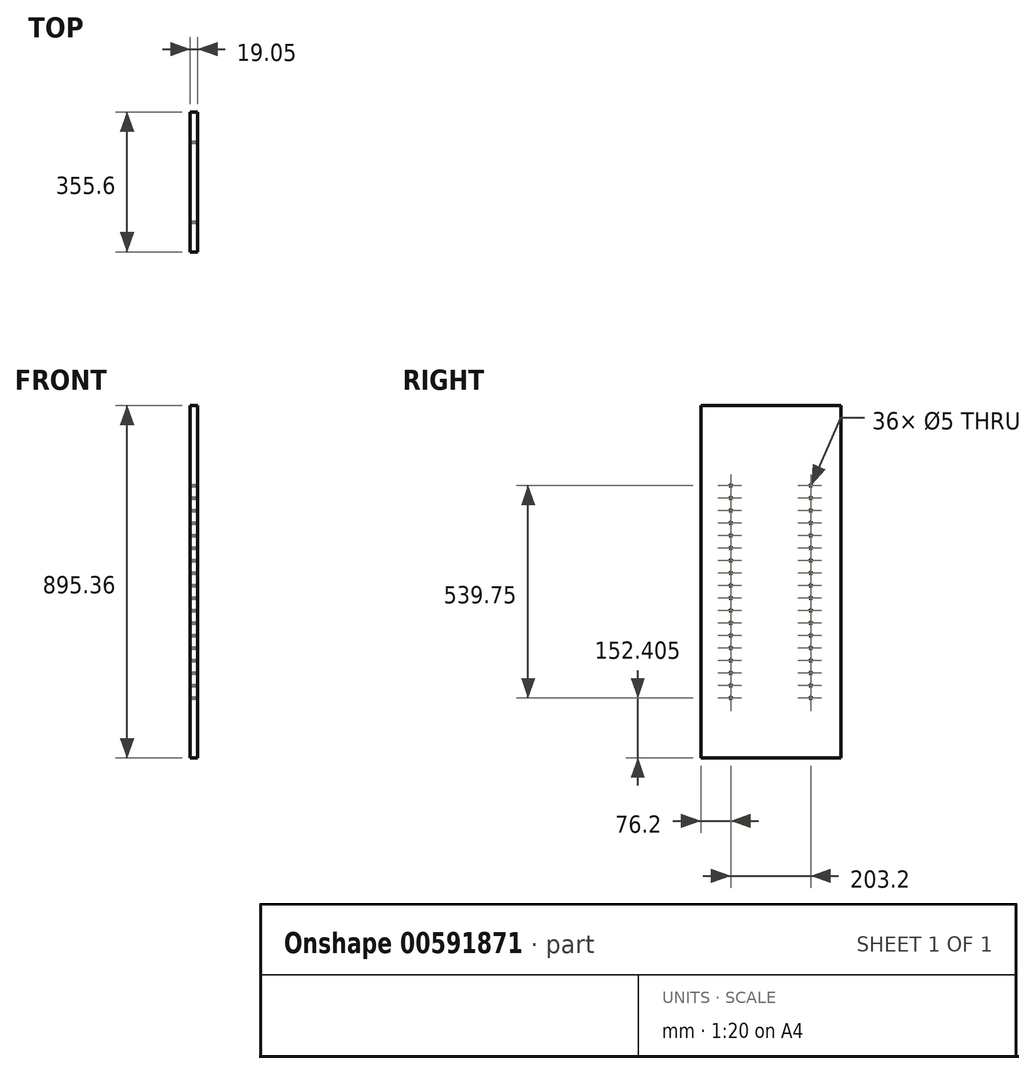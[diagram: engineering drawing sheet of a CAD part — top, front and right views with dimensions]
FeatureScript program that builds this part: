
annotation { "Feature Type Name" : "Feature", "Feature Type Description" : "" }
export const myFeature = defineFeature(function(context is Context, id is Id, definition is map)
    precondition{}
    {
        {
            var Q0;
            Q0=qCreatedBy(makeId("Right.planeOp"),FACE);
            var sketch = newSketch(context, id + "F0", { "sketchPlane" : qUnion([Q0])});
            skLineSegment(sketch, "E0.bottom", {"start": v(177.8, 447.68) * mm, "end": v(-177.8, 447.68) * mm});
            skLineSegment(sketch, "E0.top", {"start": v(177.8, -447.68) * mm, "end": v(-177.8, -447.68) * mm});
            skLineSegment(sketch, "E0.left", {"start": v(177.8, 447.68) * mm, "end": v(177.8, -447.68) * mm});
            skLineSegment(sketch, "E0.right", {"start": v(-177.8, 447.68) * mm, "end": v(-177.8, -447.68) * mm});
            skPoint(sketch, "E0.middle", {"position": v(0, 0) * mm});
            skSolve(sketch);
        }
        {
            var Q0;
            Q0=makeQuery(id+"F0.imprint","IMPRINT",FACE,{"disambiguationData":[TD([[makeQuery(id+"F0.imprint","IMPRINT",EDGE,{"derivedFrom":sQuery(id+"F0.wireOp",EDGE,"E0.bottom")}),1.0]])]});
            extrude(context, id + "F1", {"entities" : qUnion([Q0]), "depth" : 19.05 * mm, "offsetDistance" : 25.4 * mm});
        }
        {
            var Q0;
            Q0=makeQuery(id+"F1.opExtrude","CAP_FACE",FACE,{"disambiguationData":[OSD([sQuery(id+"F0.wireOp",EDGE,"E0.bottom"),sQuery(id+"F0.wireOp",EDGE,"E0.top"),sQuery(id+"F0.wireOp",EDGE,"E0.left"),sQuery(id+"F0.wireOp",EDGE,"E0.right")])],"isStart":false});
            var sketch = newSketch(context, id + "F2", { "sketchPlane" : qUnion([Q0])});
            skLineSegment(sketch, "E1", {"start": v(0, 447.68) * mm, "end": v(0, 212.73) * mm});
            skLineSegment(sketch, "E2.bottom", {"start": v(101.6, 244.48) * mm, "end": v(-101.6, 244.47) * mm});
            skLineSegment(sketch, "E2.top", {"start": v(101.6, 180.98) * mm, "end": v(-101.6, 180.98) * mm});
            skLineSegment(sketch, "E2.left", {"start": v(101.6, 244.48) * mm, "end": v(101.6, 180.98) * mm});
            skLineSegment(sketch, "E2.right", {"start": v(-101.6, 244.48) * mm, "end": v(-101.6, 180.98) * mm});
            skPoint(sketch, "E2.middle", {"position": v(0, 212.73) * mm});
            skLineSegment(sketch, "E3", {"start": v(0, 180.98) * mm, "end": v(0, 117.48) * mm});
            skLineSegment(sketch, "E4.bottom", {"start": v(101.6, 85.73) * mm, "end": v(-101.6, 85.73) * mm});
            skLineSegment(sketch, "E4.top", {"start": v(101.6, 149.23) * mm, "end": v(-101.6, 149.23) * mm});
            skLineSegment(sketch, "E4.left", {"start": v(101.6, 85.73) * mm, "end": v(101.6, 149.23) * mm});
            skLineSegment(sketch, "E4.right", {"start": v(-101.6, 85.73) * mm, "end": v(-101.6, 149.23) * mm});
            skPoint(sketch, "E4.middle", {"position": v(0, 117.48) * mm});
            skLineSegment(sketch, "E5", {"start": v(0, 85.73) * mm, "end": v(0, 22.23) * mm});
            skLineSegment(sketch, "E6.bottom", {"start": v(101.6, -9.52) * mm, "end": v(-101.6, -9.52) * mm});
            skLineSegment(sketch, "E6.top", {"start": v(101.6, 53.98) * mm, "end": v(-101.6, 53.98) * mm});
            skLineSegment(sketch, "E6.left", {"start": v(101.6, -9.52) * mm, "end": v(101.6, 53.98) * mm});
            skLineSegment(sketch, "E6.right", {"start": v(-101.6, -9.52) * mm, "end": v(-101.6, 53.98) * mm});
            skPoint(sketch, "E6.middle", {"position": v(0, 22.23) * mm});
            skLineSegment(sketch, "E7", {"start": v(0, -9.52) * mm, "end": v(0, -73.02) * mm});
            skLineSegment(sketch, "E8.bottom", {"start": v(101.6, -104.77) * mm, "end": v(-101.6, -104.77) * mm});
            skLineSegment(sketch, "E8.top", {"start": v(101.6, -41.27) * mm, "end": v(-101.6, -41.27) * mm});
            skLineSegment(sketch, "E8.left", {"start": v(101.6, -104.77) * mm, "end": v(101.6, -41.27) * mm});
            skLineSegment(sketch, "E8.right", {"start": v(-101.6, -104.77) * mm, "end": v(-101.6, -41.27) * mm});
            skPoint(sketch, "E8.middle", {"position": v(0, -73.02) * mm});
            skLineSegment(sketch, "E9", {"start": v(0, -104.77) * mm, "end": v(0, -168.27) * mm});
            skLineSegment(sketch, "E10.bottom", {"start": v(101.6, -200.02) * mm, "end": v(-101.6, -200.02) * mm});
            skLineSegment(sketch, "E10.top", {"start": v(101.6, -136.52) * mm, "end": v(-101.6, -136.52) * mm});
            skLineSegment(sketch, "E10.left", {"start": v(101.6, -200.02) * mm, "end": v(101.6, -136.52) * mm});
            skLineSegment(sketch, "E10.right", {"start": v(-101.6, -200.02) * mm, "end": v(-101.6, -136.52) * mm});
            skPoint(sketch, "E10.middle", {"position": v(0, -168.27) * mm});
            skLineSegment(sketch, "E11", {"start": v(0, -200.02) * mm, "end": v(0, -263.52) * mm});
            skPoint(sketch, "E11.endSnap0", {"position": v(0, -200.02) * mm});
            skLineSegment(sketch, "E12.bottom", {"start": v(101.6, -295.27) * mm, "end": v(-101.6, -295.27) * mm});
            skLineSegment(sketch, "E12.top", {"start": v(101.6, -231.77) * mm, "end": v(-101.6, -231.77) * mm});
            skLineSegment(sketch, "E12.left", {"start": v(101.6, -295.27) * mm, "end": v(101.6, -231.77) * mm});
            skLineSegment(sketch, "E12.right", {"start": v(-101.6, -295.27) * mm, "end": v(-101.6, -231.77) * mm});
            skPoint(sketch, "E12.middle", {"position": v(0, -263.52) * mm});
            skPoint(sketch, "E13", {"position": v(-101.6, 244.47) * mm});
            skPoint(sketch, "E14", {"position": v(-101.6, 212.73) * mm});
            skPoint(sketch, "E15", {"position": v(-101.6, 180.98) * mm});
            skPoint(sketch, "E16", {"position": v(-101.6, 149.23) * mm});
            skPoint(sketch, "E17", {"position": v(-101.6, 117.48) * mm});
            skPoint(sketch, "E18", {"position": v(-101.6, 85.73) * mm});
            skPoint(sketch, "E19", {"position": v(-101.6, 53.98) * mm});
            skPoint(sketch, "E20", {"position": v(-101.6, 22.23) * mm});
            skPoint(sketch, "E21", {"position": v(-101.6, -9.52) * mm});
            skPoint(sketch, "E22", {"position": v(-101.6, -41.27) * mm});
            skPoint(sketch, "E23", {"position": v(-101.6, -73.02) * mm});
            skPoint(sketch, "E24", {"position": v(-101.6, -104.77) * mm});
            skPoint(sketch, "E25", {"position": v(-101.6, -136.52) * mm});
            skPoint(sketch, "E26", {"position": v(-101.6, -168.27) * mm});
            skPoint(sketch, "E27", {"position": v(-101.6, -200.02) * mm});
            skPoint(sketch, "E28", {"position": v(-101.6, -231.77) * mm});
            skPoint(sketch, "E29", {"position": v(-101.6, -263.52) * mm});
            skPoint(sketch, "E30", {"position": v(-101.6, -295.27) * mm});
            skPoint(sketch, "E31", {"position": v(101.6, -295.27) * mm});
            skPoint(sketch, "E32", {"position": v(101.6, -263.52) * mm});
            skPoint(sketch, "E33", {"position": v(101.6, -231.77) * mm});
            skPoint(sketch, "E34", {"position": v(101.6, -200.02) * mm});
            skPoint(sketch, "E35", {"position": v(101.6, -168.27) * mm});
            skPoint(sketch, "E36", {"position": v(101.6, -136.52) * mm});
            skPoint(sketch, "E37", {"position": v(101.6, -104.77) * mm});
            skPoint(sketch, "E38", {"position": v(101.6, -73.02) * mm});
            skPoint(sketch, "E39", {"position": v(101.6, -41.27) * mm});
            skPoint(sketch, "E40", {"position": v(101.6, -9.52) * mm});
            skPoint(sketch, "E41", {"position": v(101.6, 22.23) * mm});
            skPoint(sketch, "E42", {"position": v(101.6, 53.98) * mm});
            skPoint(sketch, "E43", {"position": v(101.6, 85.73) * mm});
            skPoint(sketch, "E44", {"position": v(101.6, 117.48) * mm});
            skPoint(sketch, "E45", {"position": v(101.6, 149.23) * mm});
            skPoint(sketch, "E46", {"position": v(101.6, 180.98) * mm});
            skPoint(sketch, "E47", {"position": v(101.6, 212.73) * mm});
            skPoint(sketch, "E48", {"position": v(101.6, 244.48) * mm});
            skSolve(sketch);
        }
        {
            var Q0;
            Q0=sQuery(id+"F2.wireOp",VERTEX,"E13");
            var Q1;
            Q1=sQuery(id+"F2.wireOp",VERTEX,"E14");
            var Q2;
            Q2=sQuery(id+"F2.wireOp",VERTEX,"E15");
            var Q3;
            Q3=sQuery(id+"F2.wireOp",VERTEX,"E16");
            var Q4;
            Q4=sQuery(id+"F2.wireOp",VERTEX,"E18");
            var Q5;
            Q5=sQuery(id+"F2.wireOp",VERTEX,"E19");
            var Q6;
            Q6=sQuery(id+"F2.wireOp",VERTEX,"E17");
            var Q7;
            Q7=sQuery(id+"F2.wireOp",VERTEX,"E20");
            var Q8;
            Q8=sQuery(id+"F2.wireOp",VERTEX,"E21");
            var Q9;
            Q9=sQuery(id+"F2.wireOp",VERTEX,"E23");
            var Q10;
            Q10=sQuery(id+"F2.wireOp",VERTEX,"E24");
            var Q11;
            Q11=sQuery(id+"F2.wireOp",VERTEX,"E25");
            var Q12;
            Q12=sQuery(id+"F2.wireOp",VERTEX,"E25");
            var Q13;
            Q13=sQuery(id+"F2.wireOp",VERTEX,"E26");
            var Q14;
            Q14=sQuery(id+"F2.wireOp",VERTEX,"E27");
            var Q15;
            Q15=sQuery(id+"F2.wireOp",VERTEX,"E28");
            var Q16;
            Q16=sQuery(id+"F2.wireOp",VERTEX,"E29");
            var Q17;
            Q17=sQuery(id+"F2.wireOp",VERTEX,"E30");
            var Q18;
            Q18=sQuery(id+"F2.wireOp",VERTEX,"E22");
            var Q19;
            Q19=sQuery(id+"F2.wireOp",VERTEX,"E48");
            var Q20;
            Q20=sQuery(id+"F2.wireOp",VERTEX,"E47");
            var Q21;
            Q21=sQuery(id+"F2.wireOp",VERTEX,"E46");
            var Q22;
            Q22=sQuery(id+"F2.wireOp",VERTEX,"E45");
            var Q23;
            Q23=sQuery(id+"F2.wireOp",VERTEX,"E44");
            var Q24;
            Q24=sQuery(id+"F2.wireOp",VERTEX,"E43");
            var Q25;
            Q25=sQuery(id+"F2.wireOp",VERTEX,"E42");
            var Q26;
            Q26=sQuery(id+"F2.wireOp",VERTEX,"E41");
            var Q27;
            Q27=sQuery(id+"F2.wireOp",VERTEX,"E40");
            var Q28;
            Q28=sQuery(id+"F2.wireOp",VERTEX,"E39");
            var Q29;
            Q29=sQuery(id+"F2.wireOp",VERTEX,"E38");
            var Q30;
            Q30=sQuery(id+"F2.wireOp",VERTEX,"E37");
            var Q31;
            Q31=sQuery(id+"F2.wireOp",VERTEX,"E36");
            var Q32;
            Q32=sQuery(id+"F2.wireOp",VERTEX,"E35");
            var Q33;
            Q33=sQuery(id+"F2.wireOp",VERTEX,"E34");
            var Q34;
            Q34=sQuery(id+"F2.wireOp",VERTEX,"E33");
            var Q35;
            Q35=sQuery(id+"F2.wireOp",VERTEX,"E32");
            var Q36;
            Q36=sQuery(id+"F2.wireOp",VERTEX,"E31");
            var Q37;
            Q37=makeQuery(id+"F1.opExtrude","SWEPT_BODY",BODY,{"disambiguationData":[OSD([sQuery(id+"F0.wireOp",EDGE,"E0.bottom"),sQuery(id+"F0.wireOp",EDGE,"E0.top"),sQuery(id+"F0.wireOp",EDGE,"E0.left"),sQuery(id+"F0.wireOp",EDGE,"E0.right")])]});
            hole(context, id + "F3", {"style" : HoleStyle.SIMPLE, "endStyle" : HoleEndStyle.BLIND, "holeDiameter" : 5 * mm, "majorDiameter" : 6.35 * mm, "holeDepth" : 14.22 * mm, "isTappedThrough" : true, "tappedDepth" : 12.7 * mm, "tapClearance" : 3, "startFromSketch" : true, "locations" : qUnion([Q0, Q1, Q2, Q3, Q4, Q5, Q6, Q7, Q8, Q9, Q10, Q11, Q12, Q13, Q14, Q15, Q16, Q17, Q18, Q19, Q20, Q21, Q22, Q23, Q24, Q25, Q26, Q27, Q28, Q29, Q30, Q31, Q32, Q33, Q34, Q35, Q36]), "scope" : qUnion([Q37])});
        }
    });
